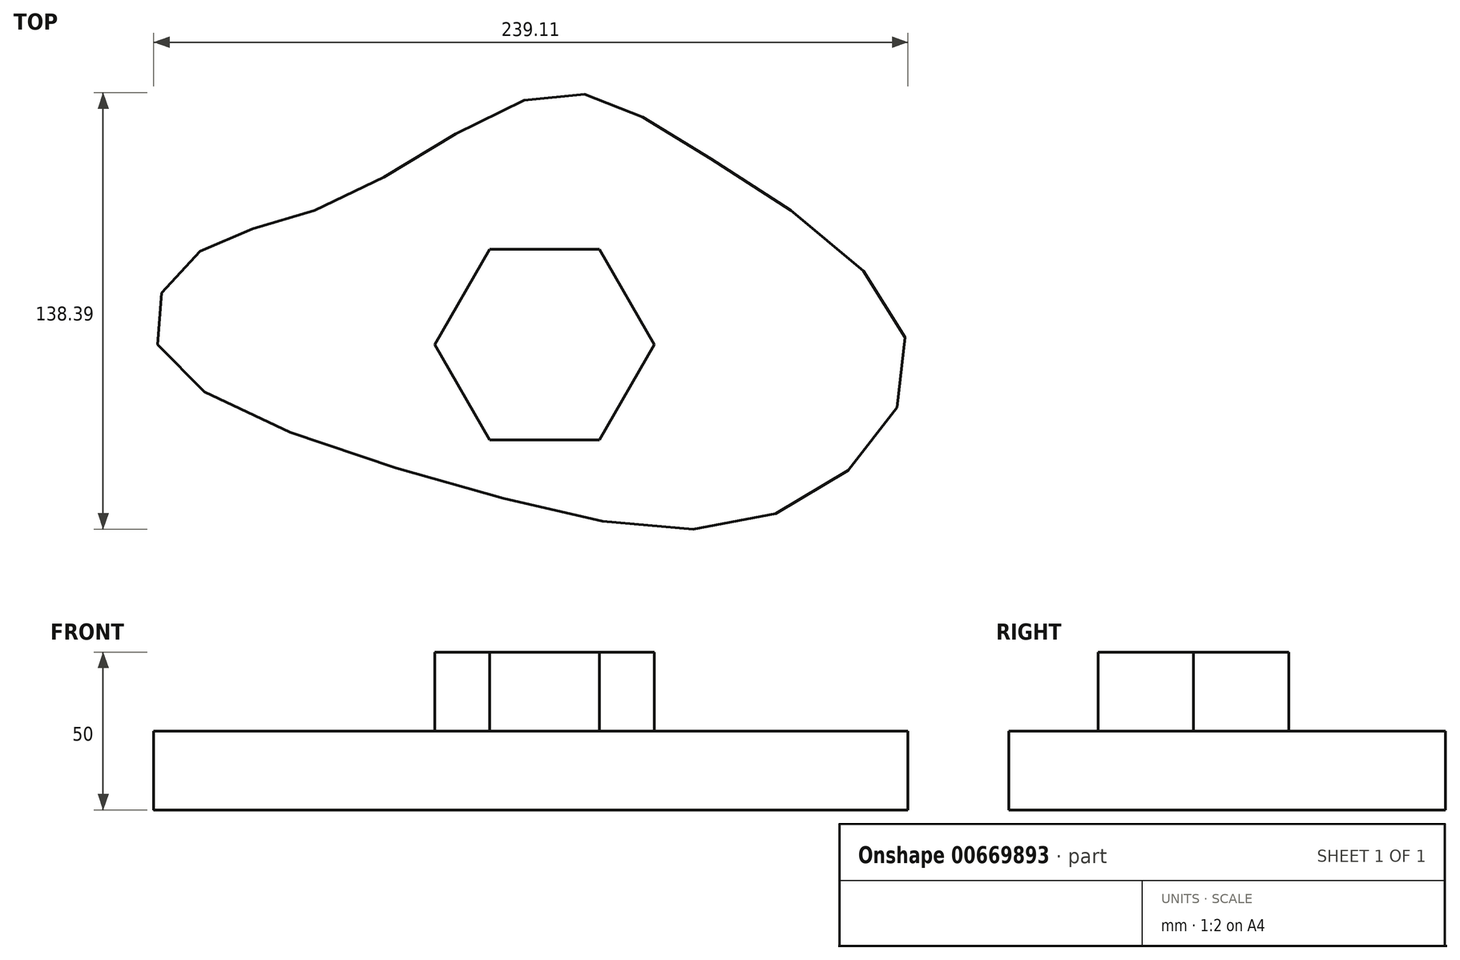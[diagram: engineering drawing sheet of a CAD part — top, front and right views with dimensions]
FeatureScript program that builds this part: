
annotation { "Feature Type Name" : "Feature", "Feature Type Description" : "" }
export const myFeature = defineFeature(function(context is Context, id is Id, definition is map)
    precondition{}
    {
        {
            var Q0;
            Q0=qCreatedBy(makeId("Top.planeOp"),FACE);
            var sketch = newSketch(context, id + "F0", { "sketchPlane" : qUnion([Q0])});
            skFitSpline(sketch, "E0", {"points": [v(-122.64, 0) * mm, v(-109.92, 29.18) * mm, v(-65.6, 45.42) * mm, v(0, 79.2) * mm, v(47.6, 62.1) * mm, v(114.75, 0) * mm, v(75.25, -52.88) * mm, v(-28.3, -44.54) * mm, v(-122.64, 0) * mm]});
            skSolve(sketch);
        }
        {
            var Q0;
            Q0=makeQuery(id+"F0.imprint","IMPRINT",FACE,{"disambiguationData":[TD([[makeQuery(id+"F0.imprint","IMPRINT",EDGE,{"derivedFrom":sQuery(id+"F0.wireOp",EDGE,"E0")}),-1.0]])]});
            extrude(context, id + "F1", {"entities" : qUnion([Q0]), "depth" : 25 * mm, "offsetDistance" : 25 * mm});
        }
        {
            var Q0;
            Q0=makeQuery(id+"F1.opExtrude","CAP_FACE",FACE,{"disambiguationData":[OSD([sQuery(id+"F0.wireOp",EDGE,"E0")])],"isStart":false});
            var sketch = newSketch(context, id + "F2", { "sketchPlane" : qUnion([Q0])});
            skCircle(sketch, "E1.cCircle", {"center": v(0, 0) * mm, "radius": 30.18 * mm, "construction": true});
            skLineSegment(sketch, "E1.0", {"start": v(-17.43, 30.18) * mm, "end": v(17.43, 30.18) * mm});
            skLineSegment(sketch, "E1.1", {"start": v(17.43, 30.18) * mm, "end": v(34.85, 0) * mm});
            skLineSegment(sketch, "E1.2", {"start": v(34.85, 0) * mm, "end": v(17.43, -30.18) * mm});
            skLineSegment(sketch, "E1.3", {"start": v(17.43, -30.18) * mm, "end": v(-17.43, -30.18) * mm});
            skLineSegment(sketch, "E1.4", {"start": v(-17.43, -30.18) * mm, "end": v(-34.85, 0) * mm});
            skLineSegment(sketch, "E1.5", {"start": v(-34.85, 0) * mm, "end": v(-17.43, 30.18) * mm});
            skPoint(sketch, "E1.0.midPoint", {"position": v(0, 30.18) * mm});
            skSolve(sketch);
        }
        {
            var Q0;
            Q0=makeQuery(id+"F2.imprint","IMPRINT",FACE,{"disambiguationData":[TD([[makeQuery(id+"F2.imprint","IMPRINT",EDGE,{"derivedFrom":sQuery(id+"F2.wireOp",EDGE,"E1.0")}),-1.0]])]});
            extrude(context, id + "F3", {"entities" : qUnion([Q0]), "operationType" : NewBodyOperationType.ADD, "depth" : 25 * mm, "offsetDistance" : 25 * mm});
        }
    });
